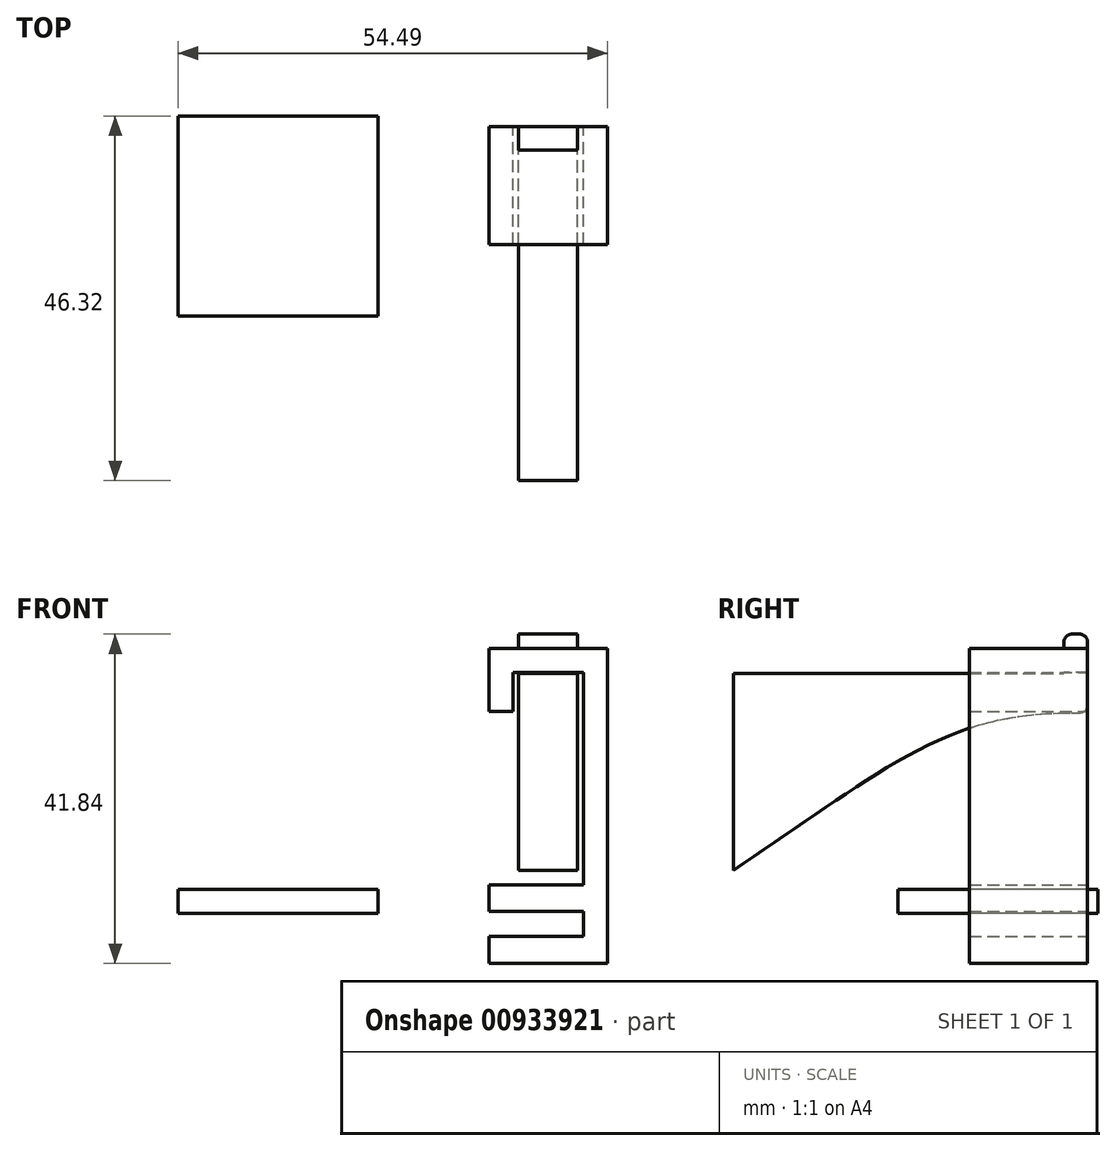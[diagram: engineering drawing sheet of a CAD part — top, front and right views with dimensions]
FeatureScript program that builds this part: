
annotation { "Feature Type Name" : "Feature", "Feature Type Description" : "" }
export const myFeature = defineFeature(function(context is Context, id is Id, definition is map)
    precondition{}
    {
        {
            var Q0;
            Q0=qCreatedBy(makeId("Front.planeOp"),FACE);
            var sketch = newSketch(context, id + "F0", { "sketchPlane" : qUnion([Q0])});
            skLineSegment(sketch, "E0.bottom", {"start": v(-31.76, 3.61) * mm, "end": v(-16.76, 3.61) * mm});
            skLineSegment(sketch, "E0.top", {"start": v(-31.76, -6.39) * mm, "end": v(-16.76, -6.39) * mm});
            skLineSegment(sketch, "E0.left", {"start": v(-31.76, 3.61) * mm, "end": v(-31.76, -6.39) * mm});
            skLineSegment(sketch, "E0.right", {"start": v(-16.76, 3.61) * mm, "end": v(-16.76, -6.39) * mm});
            skLineSegment(sketch, "E1", {"start": v(-31.76, 3.61) * mm, "end": v(-31.76, 0.21) * mm, "construction": true});
            skLineSegment(sketch, "E2.bottom", {"start": v(-31.76, 0.21) * mm, "end": v(-19.76, 0.21) * mm});
            skLineSegment(sketch, "E2.top", {"start": v(-31.76, -2.97) * mm, "end": v(-19.76, -2.97) * mm});
            skLineSegment(sketch, "E2.left", {"start": v(-31.76, 0.21) * mm, "end": v(-31.76, -2.97) * mm});
            skLineSegment(sketch, "E2.right", {"start": v(-19.76, 0.21) * mm, "end": v(-19.76, -2.97) * mm});
            skLineSegment(sketch, "E3.bottom", {"start": v(-16.76, 3.61) * mm, "end": v(-19.76, 3.61) * mm});
            skLineSegment(sketch, "E3.top", {"start": v(-16.76, 33.61) * mm, "end": v(-19.76, 33.61) * mm});
            skLineSegment(sketch, "E3.left", {"start": v(-16.76, 3.61) * mm, "end": v(-16.76, 33.61) * mm});
            skLineSegment(sketch, "E3.right", {"start": v(-19.76, 3.61) * mm, "end": v(-19.76, 33.61) * mm});
            skLineSegment(sketch, "E4.bottom", {"start": v(-19.76, 33.61) * mm, "end": v(-31.76, 33.61) * mm});
            skLineSegment(sketch, "E4.top", {"start": v(-19.76, 30.61) * mm, "end": v(-31.76, 30.61) * mm});
            skLineSegment(sketch, "E4.left", {"start": v(-19.76, 33.61) * mm, "end": v(-19.76, 30.61) * mm});
            skLineSegment(sketch, "E4.right", {"start": v(-31.76, 33.61) * mm, "end": v(-31.76, 30.61) * mm});
            skLineSegment(sketch, "E5.bottom", {"start": v(-31.76, 30.61) * mm, "end": v(-28.76, 30.61) * mm});
            skLineSegment(sketch, "E5.top", {"start": v(-31.76, 25.61) * mm, "end": v(-28.76, 25.61) * mm});
            skLineSegment(sketch, "E5.left", {"start": v(-31.76, 30.61) * mm, "end": v(-31.76, 25.61) * mm});
            skLineSegment(sketch, "E5.right", {"start": v(-28.76, 30.61) * mm, "end": v(-28.76, 25.61) * mm});
            skSolve(sketch);
        }
        {
            var Q0;
            Q0=makeQuery(id+"F0.imprint","IMPRINT",FACE,{"disambiguationData":[TD([[makeQuery(id+"F0.imprint","IMPRINT",EDGE,{"derivedFrom":sQuery(id+"F0.wireOp",EDGE,"E5.top")}),1.0]])]});
            var Q1;
            {var subQ5=sQuery(id+"F0.wireOp",EDGE,"E4.bottom");Q1=makeQuery(id+"F0.imprint","IMPRINT",FACE,{"disambiguationData":[TD([[makeQuery(id+"F0.imprint","IMPRINT",EDGE,{"derivedFrom":subQ5}),1.0]])]});}
            var Q2;
            {var subQ5=sQuery(id+"F0.wireOp",EDGE,"E3.top");Q2=makeQuery(id+"F0.imprint","IMPRINT",FACE,{"disambiguationData":[TD([[makeQuery(id+"F0.imprint","IMPRINT",EDGE,{"derivedFrom":subQ5}),1.0]])]});}
            var Q3;
            {var subQ1=sQuery(id+"F0.wireOp",EDGE,"E0.top");Q3=makeQuery(id+"F0.imprint","IMPRINT",FACE,{"disambiguationData":[TD([[makeQuery(id+"F0.imprint","IMPRINT",EDGE,{"derivedFrom":subQ1}),1.0]])]});}
            extrude(context, id + "F1", {"entities" : qUnion([Q0, Q1, Q2, Q3]), "depth" : 15 * mm, "offsetDistance" : 25 * mm});
        }
        {
            var Q0;
            Q0=qCreatedBy(makeId("Front.planeOp"),FACE);
            var sketch = newSketch(context, id + "F2", { "sketchPlane" : qUnion([Q0])});
            skLineSegment(sketch, "E6.bottom", {"start": v(-28.04, 30.45) * mm, "end": v(-20.54, 30.45) * mm});
            skLineSegment(sketch, "E6.top", {"start": v(-28.04, 25.45) * mm, "end": v(-20.54, 25.45) * mm});
            skLineSegment(sketch, "E6.left", {"start": v(-28.04, 30.45) * mm, "end": v(-28.04, 25.45) * mm});
            skLineSegment(sketch, "E6.right", {"start": v(-20.54, 30.45) * mm, "end": v(-20.54, 25.45) * mm});
            skSolve(sketch);
        }
        {
            var Q0;
            Q0 = qSketchRegion(id + "F2", true);
            extrude(context, id + "F3", {"entities" : qUnion([Q0]), "depth" : 45 * mm, "offsetDistance" : 25 * mm});
        }
        {
            var Q0;
            Q0=makeQuery(id+"F3.opExtrude","CAP_FACE",FACE,{"disambiguationData":[OSD([sQuery(id+"F2.wireOp",EDGE,"E6.bottom"),sQuery(id+"F2.wireOp",EDGE,"E6.top"),sQuery(id+"F2.wireOp",EDGE,"E6.left"),sQuery(id+"F2.wireOp",EDGE,"E6.right")])],"isStart":false});
            var sketch = newSketch(context, id + "F4", { "sketchPlane" : qUnion([Q0])});
            skLineSegment(sketch, "E7.bottom", {"start": v(-28.04, 30.45) * mm, "end": v(-20.54, 30.45) * mm});
            skLineSegment(sketch, "E7.top", {"start": v(-28.04, 5.45) * mm, "end": v(-20.54, 5.45) * mm});
            skLineSegment(sketch, "E7.left", {"start": v(-28.04, 30.45) * mm, "end": v(-28.04, 5.45) * mm});
            skLineSegment(sketch, "E7.right", {"start": v(-20.54, 30.45) * mm, "end": v(-20.54, 5.45) * mm});
            skSolve(sketch);
        }
        {
            var Q1;
            {var subQ0=sQuery(id+"F4.wireOp",EDGE,"E7.top");Q1=makeQuery(id+"F4.imprint","IMPRINT",FACE,{"disambiguationData":[TD([[makeQuery(id+"F4.imprint","IMPRINT",EDGE,{"derivedFrom":subQ0}),1.0]])]});}
            var Q2;
            Q2=makeQuery(id+"F3.opExtrude","CAP_FACE",FACE,{"disambiguationData":[OSD([sQuery(id+"F2.wireOp",EDGE,"E6.bottom"),sQuery(id+"F2.wireOp",EDGE,"E6.top"),sQuery(id+"F2.wireOp",EDGE,"E6.left"),sQuery(id+"F2.wireOp",EDGE,"E6.right")])],"isStart":true});
            loft(context, id + "F5", {"operationType" : NewBodyOperationType.ADD, "endCondition" : LoftEndDerivativeType.MATCH_CURVATURE, "endMagnitude" : 1, "sheetProfilesArray" : [{ "sheetProfileEntities" : qUnion([Q1]) }, { "sheetProfileEntities" : qUnion([Q2]) }]});
        }
        {
            var Q0;
            Q0=makeQuery(id+"F3.opExtrude","CAP_FACE",FACE,{"disambiguationData":[OSD([sQuery(id+"F2.wireOp",EDGE,"E6.bottom"),sQuery(id+"F2.wireOp",EDGE,"E6.top"),sQuery(id+"F2.wireOp",EDGE,"E6.left"),sQuery(id+"F2.wireOp",EDGE,"E6.right")])],"isStart":true});
            var sketch = newSketch(context, id + "F6", { "sketchPlane" : qUnion([Q0])});
            skLineSegment(sketch, "E8.bottom", {"start": v(20.54, 25.45) * mm, "end": v(28.04, 25.45) * mm});
            skLineSegment(sketch, "E8.top", {"start": v(20.54, 35.45) * mm, "end": v(28.04, 35.45) * mm});
            skLineSegment(sketch, "E8.left", {"start": v(20.54, 25.45) * mm, "end": v(20.54, 35.45) * mm});
            skLineSegment(sketch, "E8.right", {"start": v(28.04, 25.45) * mm, "end": v(28.04, 35.45) * mm});
            skSolve(sketch);
        }
        {
            var Q0;
            Q0 = qSketchRegion(id + "F6", true);
            extrude(context, id + "F7", {"entities" : qUnion([Q0]), "operationType" : NewBodyOperationType.ADD, "oppositeDirection" : true, "depth" : 3 * mm, "offsetDistance" : 25 * mm});
        }
        {
            var Q0;
            Q0=makeQuery(id+"F7.opExtrude","CAP_EDGE",EDGE,{"disambiguationData":[OSD([sQuery(id+"F6.wireOp",EDGE,"E8.top")])],"isStart":false});
            var Q1;
            Q1=makeQuery(id+"F7.opExtrude","CAP_EDGE",EDGE,{"disambiguationData":[OSD([sQuery(id+"F6.wireOp",EDGE,"E8.top")])],"isStart":true});
            var Q2;
            {var subQ0=sQuery(id+"F2.wireOp",EDGE,"E6.top");Q2=makeQuery(id+"F5.boolean.opBoolean","MERGE",EDGE,{"derivedFrom":[makeQuery(id+"F3.opExtrude","CAP_EDGE",EDGE,{"disambiguationData":[OSD([subQ0])],"isStart":true}),makeQuery(id+"F5.opLoft","MID_CAP_EDGE",EDGE,{"disambiguationData":[OSD([subQ0,sQuery(id+"F2.wireOp",EDGE,"E6.left"),sQuery(id+"F2.wireOp",EDGE,"E6.right")])],"capPos":1.0})]});}
            fillet(context, id + "F8", {"entities" : qUnion([Q0, Q1, Q2]), "radius" : 1 * mm, "tangentPropagation" : true, "allowEdgeOverflow" : false});
        }
        {
            var Q0;
            Q0=makeQuery(id+"F1.opExtrude","SWEPT_BODY",BODY,{"disambiguationData":[OSD([sQuery(id+"F0.wireOp",EDGE,"E0.bottom"),sQuery(id+"F0.wireOp",EDGE,"E0.top"),sQuery(id+"F0.wireOp",EDGE,"E0.left"),sQuery(id+"F0.wireOp",EDGE,"E0.right"),sQuery(id+"F0.wireOp",EDGE,"E2.bottom"),sQuery(id+"F0.wireOp",EDGE,"E2.top"),sQuery(id+"F0.wireOp",EDGE,"E2.right"),sQuery(id+"F0.wireOp",EDGE,"E3.top"),sQuery(id+"F0.wireOp",EDGE,"E3.left"),sQuery(id+"F0.wireOp",EDGE,"E3.right"),sQuery(id+"F0.wireOp",EDGE,"E4.bottom"),sQuery(id+"F0.wireOp",EDGE,"E4.top"),sQuery(id+"F0.wireOp",EDGE,"E4.right"),sQuery(id+"F0.wireOp",EDGE,"E5.top"),sQuery(id+"F0.wireOp",EDGE,"E5.left"),sQuery(id+"F0.wireOp",EDGE,"E5.right")])]});
            transform(context, id + "F9", {"entities" : qUnion([Q0]), "transformType" : TransformType.TRANSLATION_3D, "dx" : 0 * mm, "dy" : -3.9 * mm, "dz" : 0 * mm, "makeCopy" : false});
        }
        {
            var Q0;
            Q0=qCreatedBy(makeId("Top.planeOp"),FACE);
            var sketch = newSketch(context, id + "F10", { "sketchPlane" : qUnion([Q0])});
            skLineSegment(sketch, "E9.bottom", {"start": v(-71.25, -2.58) * mm, "end": v(-45.85, -2.58) * mm});
            skLineSegment(sketch, "E9.top", {"start": v(-71.25, -27.98) * mm, "end": v(-45.85, -27.98) * mm});
            skLineSegment(sketch, "E9.left", {"start": v(-71.25, -2.58) * mm, "end": v(-71.25, -27.98) * mm});
            skLineSegment(sketch, "E9.right", {"start": v(-45.85, -2.58) * mm, "end": v(-45.85, -27.98) * mm});
            skSolve(sketch);
        }
        {
            var Q0;
            Q0 = qSketchRegion(id + "F10", true);
            extrude(context, id + "F11", {"entities" : qUnion([Q0]), "depth" : 3 * mm, "offsetDistance" : 25 * mm});
        }
    });
